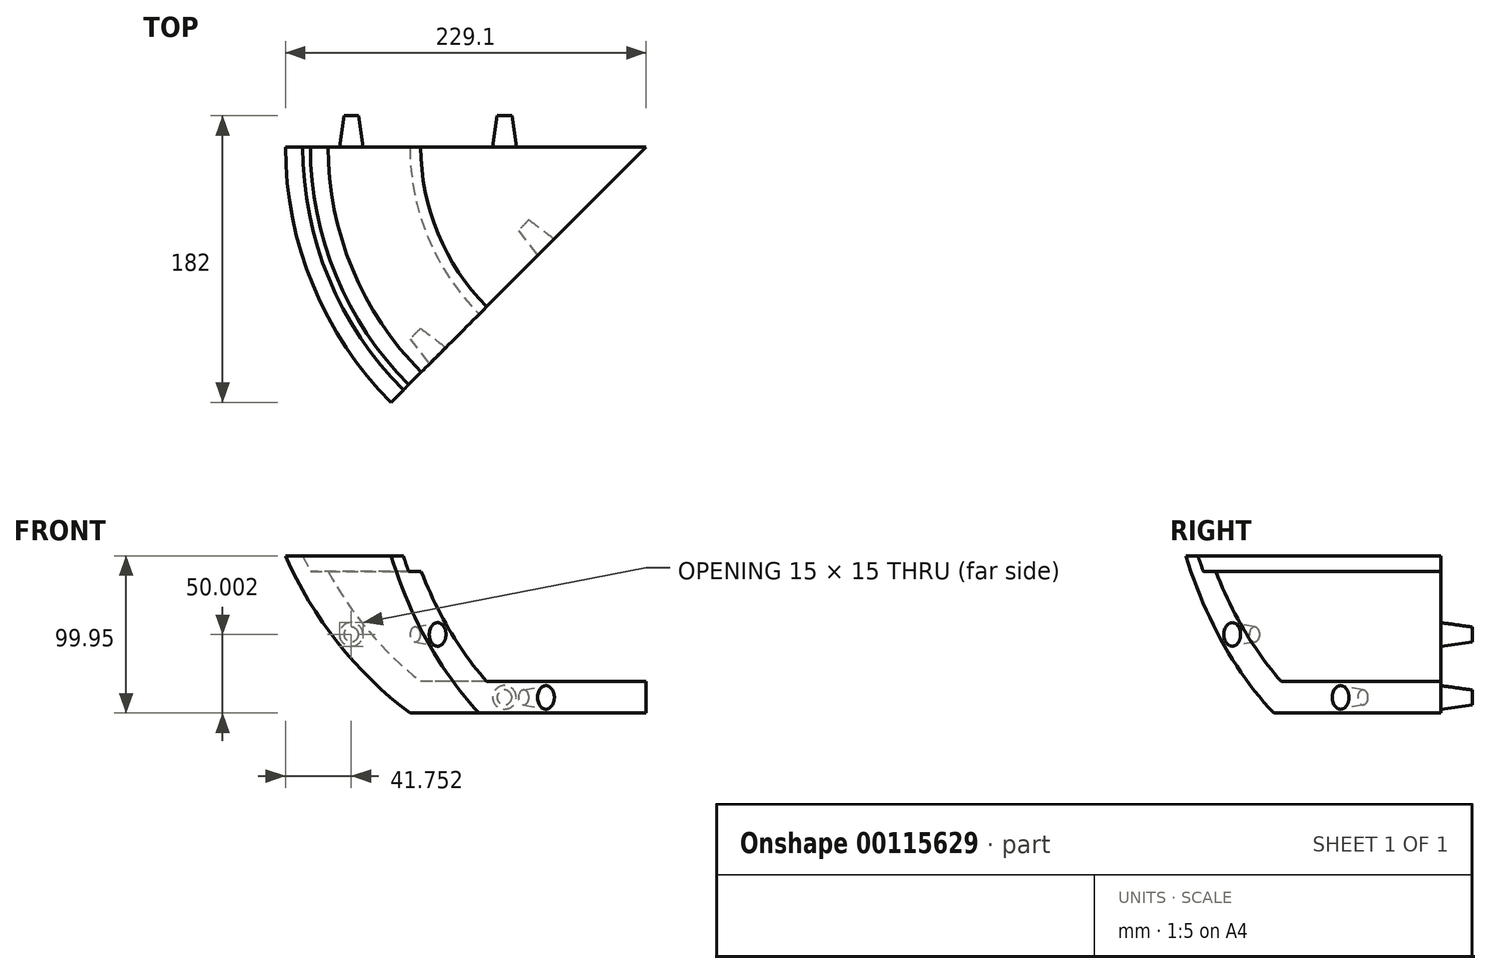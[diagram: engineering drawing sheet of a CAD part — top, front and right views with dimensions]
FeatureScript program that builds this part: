
annotation { "Feature Type Name" : "Feature", "Feature Type Description" : "" }
export const myFeature = defineFeature(function(context is Context, id is Id, definition is map)
    precondition{}
    {
        {
            var Q0;
            Q0=qCreatedBy(makeId("Front.planeOp"),FACE);
            var sketch = newSketch(context, id + "F0", { "sketchPlane" : qUnion([Q0])});
            skLineSegment(sketch, "E0", {"start": v(150.7, -275.92) * mm, "end": v(150.7, -185.92) * mm});
            skLineSegment(sketch, "E1", {"start": v(150.7, -275.92) * mm, "end": v(0.7, -275.92) * mm});
            skArc(sketch, "E2", {"start": v(-67.46, -175.97) * mm, "mid": v(-65.1, -180.97) * mm, "end": v(-62.62, -185.92) * mm});
            skLineSegment(sketch, "E3", {"start": v(-62.62, -185.92) * mm, "end": v(-62.62, -185.92) * mm});
            skLineSegment(sketch, "E4", {"start": v(-67.46, -175.97) * mm, "end": v(-78.41, -175.97) * mm});
            skArc(sketch, "E5.trimOffspring", {"start": v(-78.41, -175.97) * mm, "mid": v(-45.34, -231.07) * mm, "end": v(0.7, -275.92) * mm});
            skLineSegment(sketch, "E6", {"start": v(-62.62, -185.92) * mm, "end": v(150.7, -185.92) * mm});
            skSolve(sketch);
        }
        {
            var Q0;
            Q0 = qSketchRegion(id + "F0", true);
            var Q1;
            Q1=sQuery(id+"F0.wireOp",EDGE,"E0");
            revolve(context, id + "F1", {"entities" : qUnion([Q0]), "axis" : qUnion([Q1]), "revolveType" : RevolveType.ONE_DIRECTION, "angle" : 45 * degree});
        }
        {
            var Q0;
            Q0=makeQuery(id+"F1.opRevolve","CAP_FACE",FACE,{"disambiguationData":[OSD([sQuery(id+"F0.wireOp",EDGE,"E0"),sQuery(id+"F0.wireOp",EDGE,"E1"),sQuery(id+"F0.wireOp",EDGE,"f9b69b49-8556-4f17-9e22-db1f233e9ffd"),sQuery(id+"F0.wireOp",EDGE,"E2"),sQuery(id+"F0.wireOp",EDGE,"E3"),sQuery(id+"F0.wireOp",EDGE,"f335859e-29cc-4bce-a6e0-b7dbcc9f62ed"),sQuery(id+"F0.wireOp",EDGE,"E4"),sQuery(id+"F0.wireOp",EDGE,"942f9dd1-8637-4c1f-bec1-97d13f12d993.trimOffspring"),sQuery(id+"F0.wireOp",EDGE,"E5.trimOffspring")])],"isStart":false});
            var Q1;
            Q1=makeQuery(id+"F1.opRevolve","SWEPT_FACE",FACE,{"disambiguationData":[OSD([sQuery(id+"F0.wireOp",EDGE,"f9b69b49-8556-4f17-9e22-db1f233e9ffd")])]});
            var Q2;
            Q2=makeQuery(id+"F1.opRevolve","CAP_FACE",FACE,{"disambiguationData":[OSD([sQuery(id+"F0.wireOp",EDGE,"E0"),sQuery(id+"F0.wireOp",EDGE,"E1"),sQuery(id+"F0.wireOp",EDGE,"f9b69b49-8556-4f17-9e22-db1f233e9ffd"),sQuery(id+"F0.wireOp",EDGE,"E2"),sQuery(id+"F0.wireOp",EDGE,"E3"),sQuery(id+"F0.wireOp",EDGE,"f335859e-29cc-4bce-a6e0-b7dbcc9f62ed"),sQuery(id+"F0.wireOp",EDGE,"E4"),sQuery(id+"F0.wireOp",EDGE,"942f9dd1-8637-4c1f-bec1-97d13f12d993.trimOffspring"),sQuery(id+"F0.wireOp",EDGE,"E5.trimOffspring")])],"isStart":true});
            var Q3;
            Q3=makeQuery(id+"F1.opRevolve","SWEPT_FACE",FACE,{"disambiguationData":[OSD([sQuery(id+"F0.wireOp",EDGE,"E6")])]});
            shell(context, id + "F2", {"entities" : qUnion([Q0, Q1, Q2, Q3]), "thickness" : 20 * mm});
        }
        {
            var Q0;
            Q0=makeQuery(id+"F1.opRevolve","CAP_FACE",FACE,{"disambiguationData":[OSD([sQuery(id+"F0.wireOp",EDGE,"E0"),sQuery(id+"F0.wireOp",EDGE,"E1"),sQuery(id+"F0.wireOp",EDGE,"f9b69b49-8556-4f17-9e22-db1f233e9ffd"),sQuery(id+"F0.wireOp",EDGE,"E2"),sQuery(id+"F0.wireOp",EDGE,"E3"),sQuery(id+"F0.wireOp",EDGE,"f335859e-29cc-4bce-a6e0-b7dbcc9f62ed"),sQuery(id+"F0.wireOp",EDGE,"E4"),sQuery(id+"F0.wireOp",EDGE,"942f9dd1-8637-4c1f-bec1-97d13f12d993.trimOffspring"),sQuery(id+"F0.wireOp",EDGE,"E5.trimOffspring")])],"isStart":false});
            var sketch = newSketch(context, id + "F3", { "sketchPlane" : qUnion([Q0])});
            skCircle(sketch, "E7", {"center": v(-80.8, -225.92) * mm, "radius": 7.5 * mm});
            skCircle(sketch, "E8", {"center": v(16.56, -265.92) * mm, "radius": 7.5 * mm});
            skSolve(sketch);
        }
        {
            var Q0;
            Q0 = qSketchRegion(id + "F3", true);
            extrude(context, id + "F4", {"entities" : qUnion([Q0]), "operationType" : NewBodyOperationType.REMOVE, "oppositeDirection" : true, "depth" : 20 * mm, "hasDraft" : true, "draftAngle" : 8 * degree, "draftPullDirection" : true});
        }
        {
            var Q0;
            Q0=makeQuery(id+"F1.opRevolve","CAP_FACE",FACE,{"disambiguationData":[OSD([sQuery(id+"F0.wireOp",EDGE,"E0"),sQuery(id+"F0.wireOp",EDGE,"E1"),sQuery(id+"F0.wireOp",EDGE,"f9b69b49-8556-4f17-9e22-db1f233e9ffd"),sQuery(id+"F0.wireOp",EDGE,"E2"),sQuery(id+"F0.wireOp",EDGE,"E3"),sQuery(id+"F0.wireOp",EDGE,"f335859e-29cc-4bce-a6e0-b7dbcc9f62ed"),sQuery(id+"F0.wireOp",EDGE,"E4"),sQuery(id+"F0.wireOp",EDGE,"942f9dd1-8637-4c1f-bec1-97d13f12d993.trimOffspring"),sQuery(id+"F0.wireOp",EDGE,"E5.trimOffspring")])],"isStart":true});
            var sketch = newSketch(context, id + "F5", { "sketchPlane" : qUnion([Q0])});
            skCircle(sketch, "E9", {"center": v(-60.7, -265.92) * mm, "radius": 7.5 * mm});
            skCircle(sketch, "E10", {"center": v(36.66, -225.92) * mm, "radius": 7.5 * mm});
            skSolve(sketch);
        }
        {
            var Q0;
            Q0=makeQuery(id+"F5.imprint","IMPRINT",FACE,{"disambiguationData":[TD([[makeQuery(id+"F5.imprint","IMPRINT",EDGE,{"derivedFrom":sQuery(id+"F5.wireOp",EDGE,"E9")}),1.0]])]});
            var Q1;
            Q1=makeQuery(id+"F5.imprint","IMPRINT",FACE,{"disambiguationData":[TD([[makeQuery(id+"F5.imprint","IMPRINT",EDGE,{"derivedFrom":sQuery(id+"F5.wireOp",EDGE,"E10")}),1.0]])]});
            extrude(context, id + "F6", {"entities" : qUnion([Q0, Q1]), "operationType" : NewBodyOperationType.ADD, "depth" : 20 * mm, "hasDraft" : true, "draftAngle" : 8 * degree, "draftPullDirection" : true});
        }
        {
            var Q0;
            Q0=makeQuery(id+"F1.opRevolve","SWEPT_BODY",BODY,{"disambiguationData":[OSD([sQuery(id+"F0.wireOp",EDGE,"E0"),sQuery(id+"F0.wireOp",EDGE,"E1"),sQuery(id+"F0.wireOp",EDGE,"E2"),sQuery(id+"F0.wireOp",EDGE,"E4"),sQuery(id+"F0.wireOp",EDGE,"E5.trimOffspring"),sQuery(id+"F0.wireOp",EDGE,"E6")])]});
            transform(context, id + "F7", {"entities" : qUnion([Q0]), "transformType" : TransformType.COPY});
        }
    });
